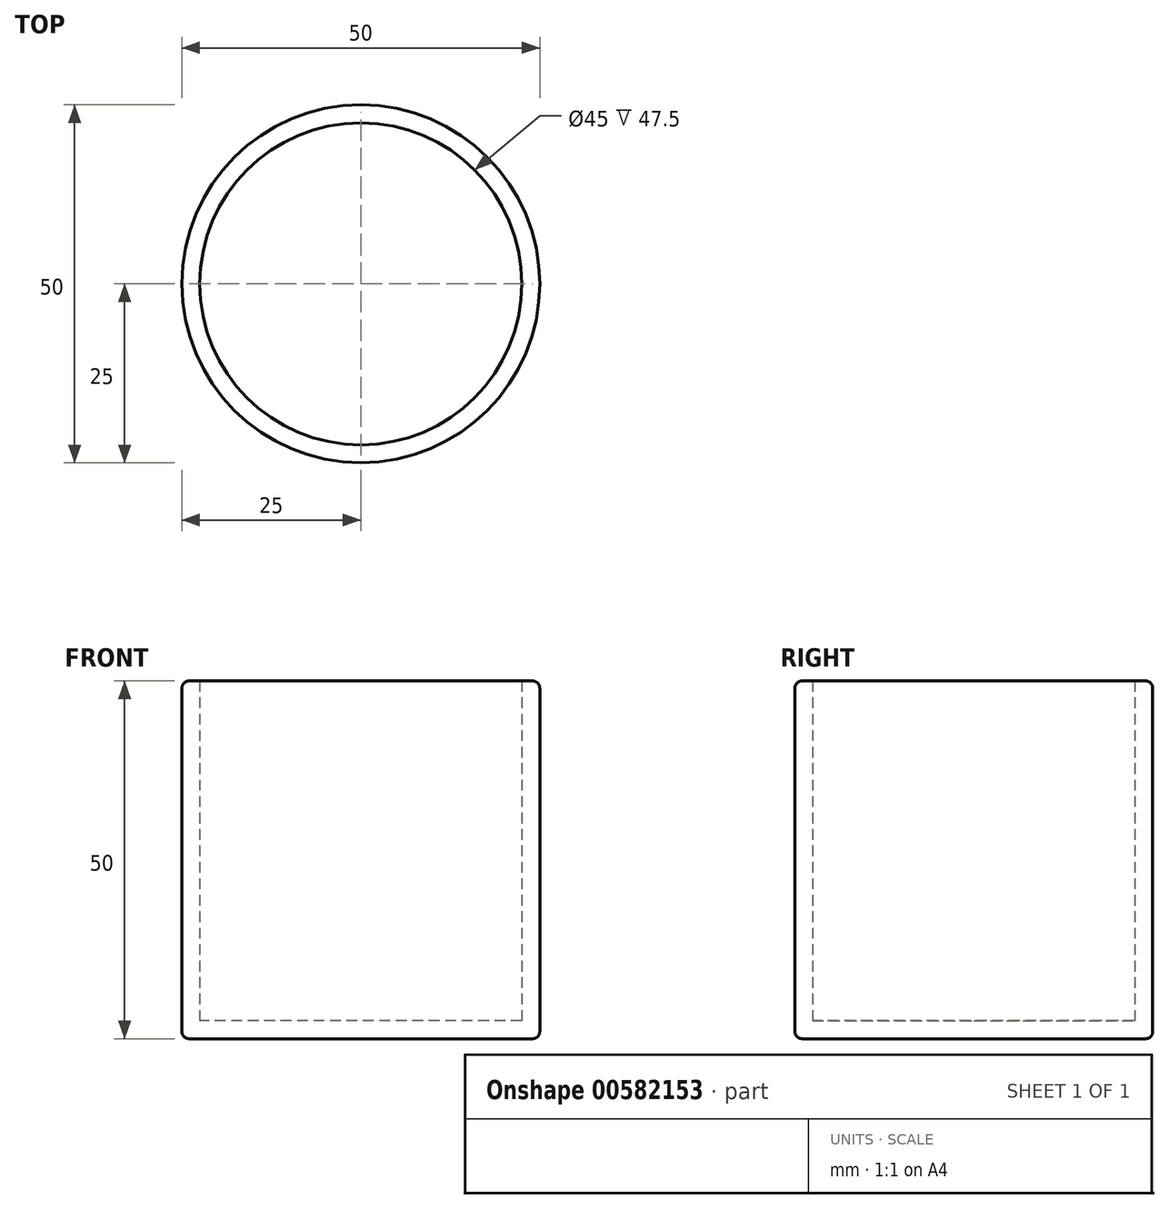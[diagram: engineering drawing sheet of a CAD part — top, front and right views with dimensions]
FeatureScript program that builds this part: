
annotation { "Feature Type Name" : "Feature", "Feature Type Description" : "" }
export const myFeature = defineFeature(function(context is Context, id is Id, definition is map)
    precondition{}
    {
        {
            var Q0;
            Q0=qCreatedBy(makeId("Top.planeOp"),FACE);
            var sketch = newSketch(context, id + "F0", { "sketchPlane" : qUnion([Q0])});
            skCircle(sketch, "E0", {"center": v(0, 0) * mm, "radius": 25 * mm});
            skSolve(sketch);
        }
        {
            var Q0;
            Q0 = qSketchRegion(id + "F0", true);
            extrude(context, id + "F1", {"entities" : qUnion([Q0]), "depth" : 50 * mm, "offsetDistance" : 25 * mm});
        }
        {
            var Q0;
            Q0=makeQuery(id+"F1.opExtrude","CAP_FACE",FACE,{"disambiguationData":[OSD([sQuery(id+"F0.wireOp",EDGE,"E0")])],"isStart":false});
            shell(context, id + "F2", {"entities" : qUnion([Q0]), "thickness" : 2.5 * mm});
        }
        {
            var Q0;
            Q0=makeQuery(id+"F1.opExtrude","SWEPT_FACE",FACE,{"disambiguationData":[OSD([sQuery(id+"F0.wireOp",EDGE,"E0")])]});
            fillet(context, id + "F3", {"entities" : qUnion([Q0]), "radius" : 1 * mm, "tangentPropagation" : true, "allowEdgeOverflow" : false});
        }
    });
